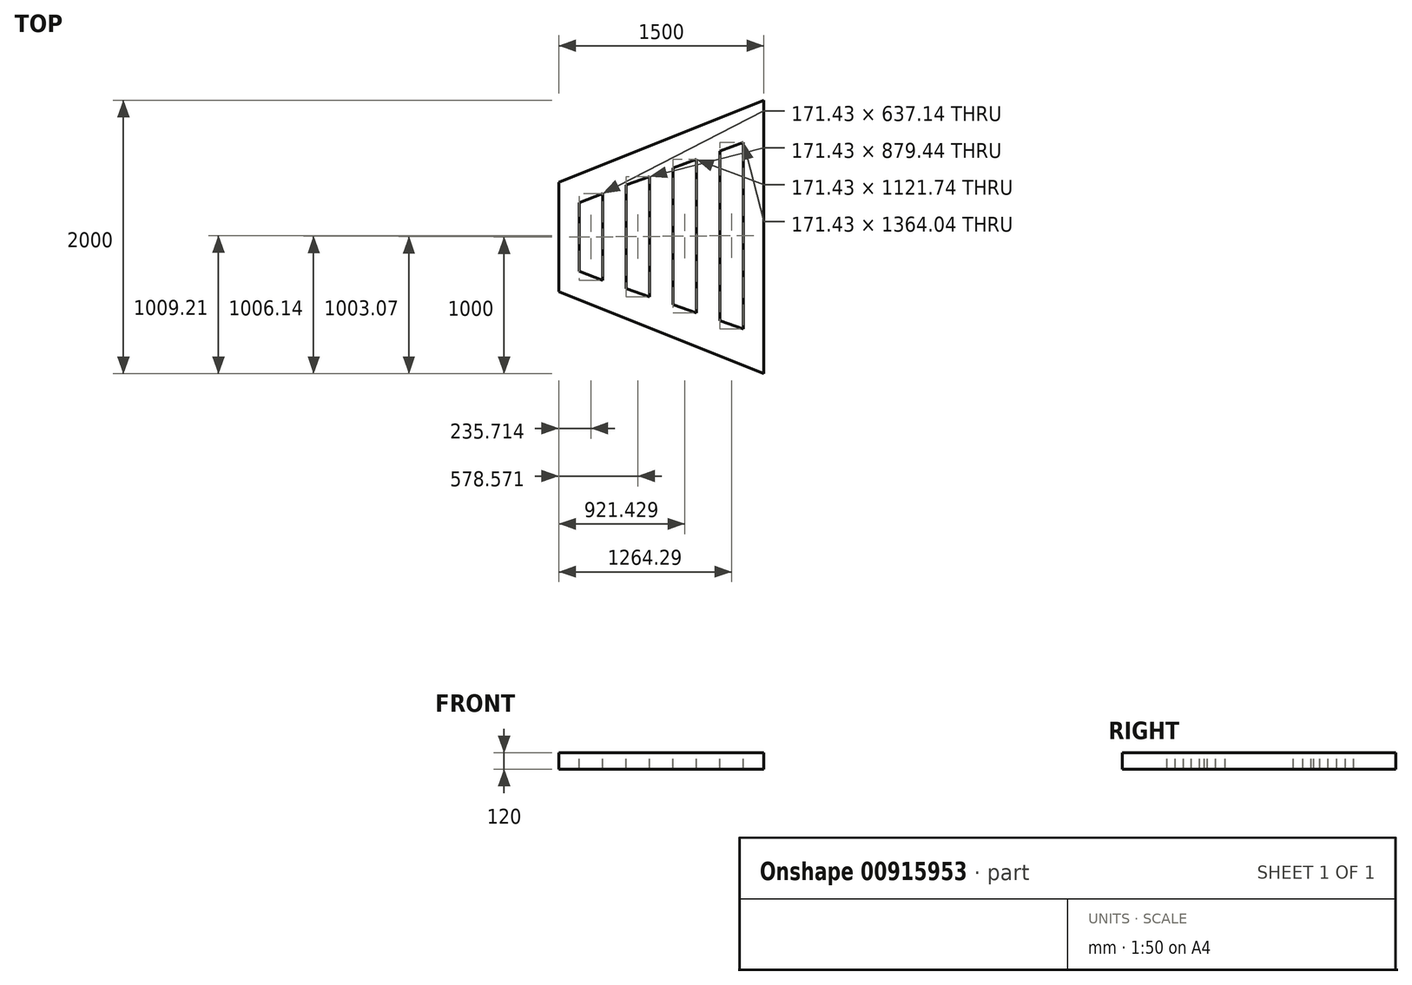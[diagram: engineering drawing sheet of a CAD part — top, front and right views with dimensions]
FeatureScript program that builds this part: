
annotation { "Feature Type Name" : "Feature", "Feature Type Description" : "" }
export const myFeature = defineFeature(function(context is Context, id is Id, definition is map)
    precondition{}
    {
        {
            var Q0;
            Q0=qCreatedBy(makeId("Top.planeOp"),FACE);
            var sketch = newSketch(context, id + "F0", { "sketchPlane" : qUnion([Q0])});
            skLineSegment(sketch, "E0", {"start": v(0, 1000) * mm, "end": v(0, -1000) * mm});
            skLineSegment(sketch, "E1", {"start": v(-1500, 400) * mm, "end": v(-1500, -400) * mm});
            skLineSegment(sketch, "E2", {"start": v(-1500, 400) * mm, "end": v(0, 1000) * mm});
            skLineSegment(sketch, "E3", {"start": v(-1500, -400) * mm, "end": v(0, -1000) * mm});
            skLineSegment(sketch, "E4", {"start": v(-1350, 250) * mm, "end": v(-1350, -250) * mm});
            skLineSegment(sketch, "E5", {"start": v(-1350, -250) * mm, "end": v(-1178.57, -318.57) * mm});
            skLineSegment(sketch, "E6", {"start": v(-1178.57, 318.57) * mm, "end": v(-1178.57, -318.57) * mm});
            skLineSegment(sketch, "E7.trimOffspring", {"start": v(-1178.57, 318.57) * mm, "end": v(-1350, 250) * mm});
            skLineSegment(sketch, "E8", {"start": v(-150, 691.23) * mm, "end": v(-321.43, 629.12) * mm});
            skLineSegment(sketch, "E9", {"start": v(-150, 691.23) * mm, "end": v(-150, -672.81) * mm});
            skLineSegment(sketch, "E10", {"start": v(-1007.14, -377.61) * mm, "end": v(-835.71, -436.65) * mm});
            skLineSegment(sketch, "E11", {"start": v(-1007.14, 380.68) * mm, "end": v(-1007.14, -377.61) * mm});
            skLineSegment(sketch, "E12", {"start": v(-835.71, 442.79) * mm, "end": v(-835.71, -436.65) * mm});
            skLineSegment(sketch, "E13", {"start": v(-664.29, 504.9) * mm, "end": v(-664.29, -495.7) * mm});
            skLineSegment(sketch, "E14", {"start": v(-492.86, 567) * mm, "end": v(-492.86, -554.73) * mm});
            skLineSegment(sketch, "E15", {"start": v(-321.43, 629.12) * mm, "end": v(-321.43, -613.77) * mm});
            skLineSegment(sketch, "E16.trimOffspring", {"start": v(-835.71, 442.79) * mm, "end": v(-1007.14, 380.68) * mm});
            skLineSegment(sketch, "E17.trimOffspring", {"start": v(-664.29, -495.7) * mm, "end": v(-492.86, -554.73) * mm});
            skLineSegment(sketch, "E18.trimOffspring", {"start": v(-492.86, 567) * mm, "end": v(-664.29, 504.9) * mm});
            skLineSegment(sketch, "E19.trimOffspring", {"start": v(-321.43, -613.77) * mm, "end": v(-150, -672.81) * mm});
            skSolve(sketch);
        }
        {
            var Q0;
            Q0 = qSketchRegion(id + "F0", true);
            extrude(context, id + "F1", {"entities" : qUnion([Q0]), "oppositeDirection" : true, "depth" : 120 * mm, "offsetDistance" : 25 * mm});
        }
        {
            var Q0;
            Q0=makeQuery(id+"F1.opExtrude","SWEPT_FACE",FACE,{"disambiguationData":[OSD([sQuery(id+"F0.wireOp",EDGE,"E1")])]});
            cPlane(context, id + "F2", {"entities" : qUnion([Q0]), "cplaneType" : CPlaneType.OFFSET, "offset" : 0 * mm, "width" : 150 * mm, "height" : 150 * mm});
        }
        {
            var Q0;
            Q0 = qSketchRegion(id + "F0", true);
            extrude(context, id + "F3", {"entities" : qUnion([Q0]), "operationType" : NewBodyOperationType.ADD, "oppositeDirection" : true, "depth" : 120 * mm, "offsetDistance" : 25 * mm});
        }
    });
